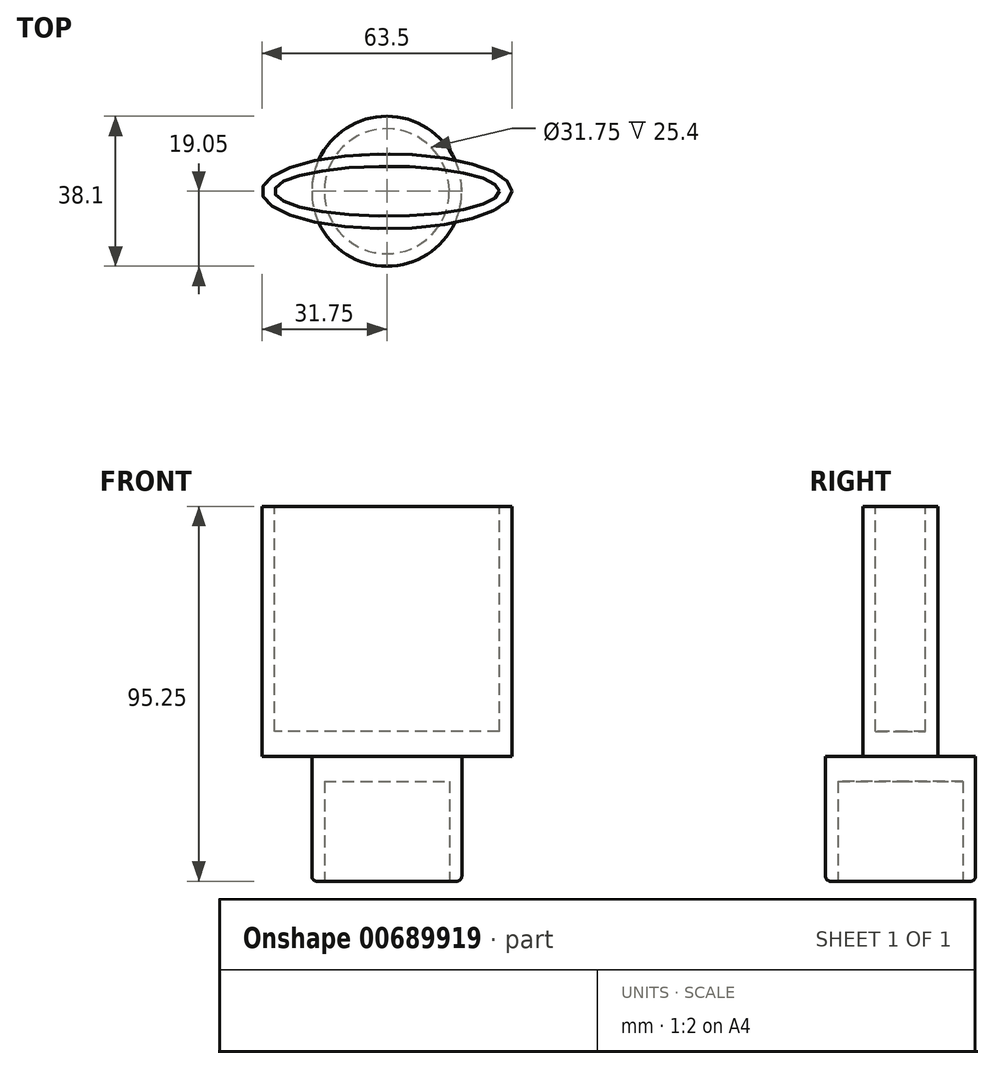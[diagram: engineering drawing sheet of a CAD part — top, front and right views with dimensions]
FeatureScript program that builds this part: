
annotation { "Feature Type Name" : "Feature", "Feature Type Description" : "" }
export const myFeature = defineFeature(function(context is Context, id is Id, definition is map)
    precondition{}
    {
        {
            var Q0;
            Q0=qCreatedBy(makeId("Top.planeOp"),FACE);
            var sketch = newSketch(context, id + "F0", { "sketchPlane" : qUnion([Q0])});
            skEllipse(sketch, "E0", {"center": v(0, 0) * mm, "majorRadius": 31.75 * mm, "minorRadius": 9.53 * mm, "majorAxis": v(1, 0)});
            skCircle(sketch, "E1", {"center": v(0, 0) * mm, "radius": 15.88 * mm});
            skSolve(sketch);
        }
        {
            var Q0;
            {var subQ0=sQuery(id+"F0.wireOp",EDGE,"E1");var subQ1=sQuery(id+"F0.wireOp",EDGE,"E0");var subQ2=makeQuery(id+"F0.imprint","INTERSECT",VERTEX,{"disambiguationData":[OD(0.0)],"derivedFrom":[subQ1,subQ0]});Q0=makeQuery(id+"F0.imprint","IMPRINT",FACE,{"disambiguationData":[TD([[makeQuery(id+"F0.imprint","IMPRINT",EDGE,{"disambiguationData":[TD([[subQ2,-1.0]])],"derivedFrom":subQ1}),1.0]])]});}
            var Q1;
            {var subQ0=sQuery(id+"F0.wireOp",EDGE,"E1");var subQ1=sQuery(id+"F0.wireOp",EDGE,"E0");var subQ2=makeQuery(id+"F0.imprint","INTERSECT",VERTEX,{"disambiguationData":[OD(0.0)],"derivedFrom":[subQ1,subQ0]});Q1=makeQuery(id+"F0.imprint","IMPRINT",FACE,{"disambiguationData":[TD([[makeQuery(id+"F0.imprint","IMPRINT",EDGE,{"disambiguationData":[TD([[subQ2,1.0]])],"derivedFrom":subQ1}),1.0]])]});}
            var Q2;
            {var subQ0=sQuery(id+"F0.wireOp",EDGE,"E1");var subQ1=sQuery(id+"F0.wireOp",EDGE,"E0");var subQ2=makeQuery(id+"F0.imprint","INTERSECT",VERTEX,{"disambiguationData":[OD(1.0)],"derivedFrom":[subQ1,subQ0]});Q2=makeQuery(id+"F0.imprint","IMPRINT",FACE,{"disambiguationData":[TD([[makeQuery(id+"F0.imprint","IMPRINT",EDGE,{"disambiguationData":[TD([[subQ2,1.0]])],"derivedFrom":subQ1}),1.0]])]});}
            extrude(context, id + "F1", {"entities" : qUnion([Q0, Q1, Q2]), "depth" : 63.5 * mm, "offsetDistance" : 25.4 * mm});
        }
        {
            var Q0;
            Q0=qCreatedBy(makeId("Top.planeOp"),FACE);
            var sketch = newSketch(context, id + "F2", { "sketchPlane" : qUnion([Q0])});
            skCircle(sketch, "E2", {"center": v(0, 0) * mm, "radius": 19.05 * mm});
            skSolve(sketch);
        }
        {
            var Q0;
            Q0=makeQuery(id+"F2.imprint","IMPRINT",FACE,{"disambiguationData":[TD([[makeQuery(id+"F2.imprint","IMPRINT",EDGE,{"derivedFrom":sQuery(id+"F2.wireOp",EDGE,"E2")}),1.0]])]});
            extrude(context, id + "F3", {"entities" : qUnion([Q0]), "operationType" : NewBodyOperationType.ADD, "oppositeDirection" : true, "depth" : 31.75 * mm, "offsetDistance" : 25.4 * mm});
        }
        {
            var Q0;
            Q0=makeQuery(id+"F3.opExtrude","CAP_FACE",FACE,{"disambiguationData":[OSD([sQuery(id+"F2.wireOp",EDGE,"E2")])],"isStart":false});
            var sketch = newSketch(context, id + "F4", { "sketchPlane" : qUnion([Q0])});
            skCircle(sketch, "E3", {"center": v(0, 0) * mm, "radius": 15.88 * mm});
            skSolve(sketch);
        }
        {
            var Q0;
            Q0=makeQuery(id+"F4.imprint","IMPRINT",FACE,{"disambiguationData":[TD([[makeQuery(id+"F4.imprint","IMPRINT",EDGE,{"derivedFrom":sQuery(id+"F4.wireOp",EDGE,"E3")}),1.0]])]});
            extrude(context, id + "F5", {"entities" : qUnion([Q0]), "operationType" : NewBodyOperationType.REMOVE, "oppositeDirection" : true, "depth" : 25.4 * mm, "offsetDistance" : 25.4 * mm});
        }
        {
            var Q0;
            Q0=makeQuery(id+"F1.opExtrude","CAP_FACE",FACE,{"disambiguationData":[OSD([sQuery(id+"F0.wireOp",EDGE,"E0")])],"isStart":false});
            var sketch = newSketch(context, id + "F6", { "sketchPlane" : qUnion([Q0])});
            skSolve(sketch);
        }
        {
            var Q0;
            Q0=makeQuery(id+"F6.imprint","IMPRINT",FACE,{"disambiguationData":[TD([[makeQuery(id+"F6.imprint","IMPRINT",EDGE,{"derivedFrom":makeQuery(id+"F1.opExtrude","CAP_EDGE",EDGE,{"disambiguationData":[OSD([sQuery(id+"F0.wireOp",EDGE,"E0")])],"isStart":false})}),1.0]])]});
            var sketch = newSketch(context, id + "F7", { "sketchPlane" : qUnion([Q0])});
            skEllipse(sketch, "E4", {"center": v(0, 0) * mm, "majorRadius": 28.58 * mm, "minorRadius": 6.35 * mm, "majorAxis": v(1, 0)});
            skSolve(sketch);
        }
        {
            var Q0;
            Q0=makeQuery(id+"F7.imprint","IMPRINT",FACE,{"disambiguationData":[TD([[makeQuery(id+"F7.imprint","IMPRINT",EDGE,{"derivedFrom":sQuery(id+"F7.wireOp",EDGE,"E4")}),1.0]])]});
            extrude(context, id + "F8", {"entities" : qUnion([Q0]), "operationType" : NewBodyOperationType.REMOVE, "oppositeDirection" : true, "depth" : 57.15 * mm, "offsetDistance" : 25.4 * mm});
        }
        {
            var Q0;
            Q0=makeQuery(id+"F3.opExtrude","CAP_EDGE",EDGE,{"disambiguationData":[OSD([sQuery(id+"F2.wireOp",EDGE,"E2")])],"isStart":false});
            fillet(context, id + "F9", {"entities" : qUnion([Q0]), "radius" : 1.27 * mm, "tangentPropagation" : true, "allowEdgeOverflow" : false});
        }
    });
